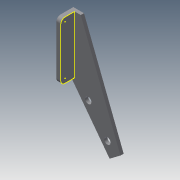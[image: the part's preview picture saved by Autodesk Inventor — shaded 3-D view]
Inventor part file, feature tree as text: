
AUTODESK INVENTOR PART (.ipt)
format: ipt  version: 2013 (Build 170138000, 138)  size: 161,280 bytes
history: native  units: mm
features: sketch x16, extrude x8, fillet x2
ambient origin geometry x8: Origin, YZ Plane, XZ Plane, XY Plane, X Axis, Y Axis, Z Axis, Center Point
bodies: Solid1 (feature_tree)
feature tree (26):
  sketch  "Sketch1"  dims[d4=3.0mm d5=3.0mm d6=2.0mm d7=0.0mm]
  extrude  "Extrusion1"  Depth=2.0mm TaperAngle=0.0deg
  extrude  "Extrusion2"  Depth=2.0mm TaperAngle=0.0deg
  extrude  "Extrusion3"  Depth=2.0mm TaperAngle=0.0deg
  sketch  "Sketch5"  dims[d19=0.5mm d20=0.0mm d21=10.0mm]
  extrude  "Extrusion4"  Depth=6.0mm TaperAngle=0.0deg
  sketch  "Sketch7"  dims[d25=1.5mm d26=0.0mm d27=10.0mm d28=0.0mm]
  sketch  "Sketch8"  dims[d29=2.0mm d30=2.0mm]
  extrude  "Extrusion5"  Depth=10.0mm
  sketch  "Sketch10"
  extrude  "Extrusion6"  Depth=1.5mm TaperAngle=0.0deg
  extrude  "Extrusion7"  Depth=10.0mm TaperAngle=0.0deg
  extrude  "Extrusion8"  Depth=2.0mm
  fillet  "Fillet1"  [1 undecoded]
  fillet  "Fillet2"  [1 undecoded]
  sketch  "Sketch14"
  sketch  "Sketch15"
  sketch  "Sketch16"
  sketch  "Sketch2"  dims[d8=10.0mm d11=2.0mm d12=0.0mm]
  sketch  "Sketch3"  dims[d13=5.0mm d14=2.0mm d15=0.0mm]
  sketch  "Sketch4"  dims[d16=2.0mm d17=6.0mm d18=0.0mm]
  sketch  "Sketch6"  dims[d22=5.0mm d23=1.5mm d24=0.0mm]
  sketch  "Sketch9"
  sketch  "Sketch11"
  sketch  "Sketch12"
  sketch  "Sketch13"
note: 2 required parameter values undecoded (feature->parameter linkage not recoverable at this tier; creation-order binding heuristic only, values carry confidence <= 0.55)
